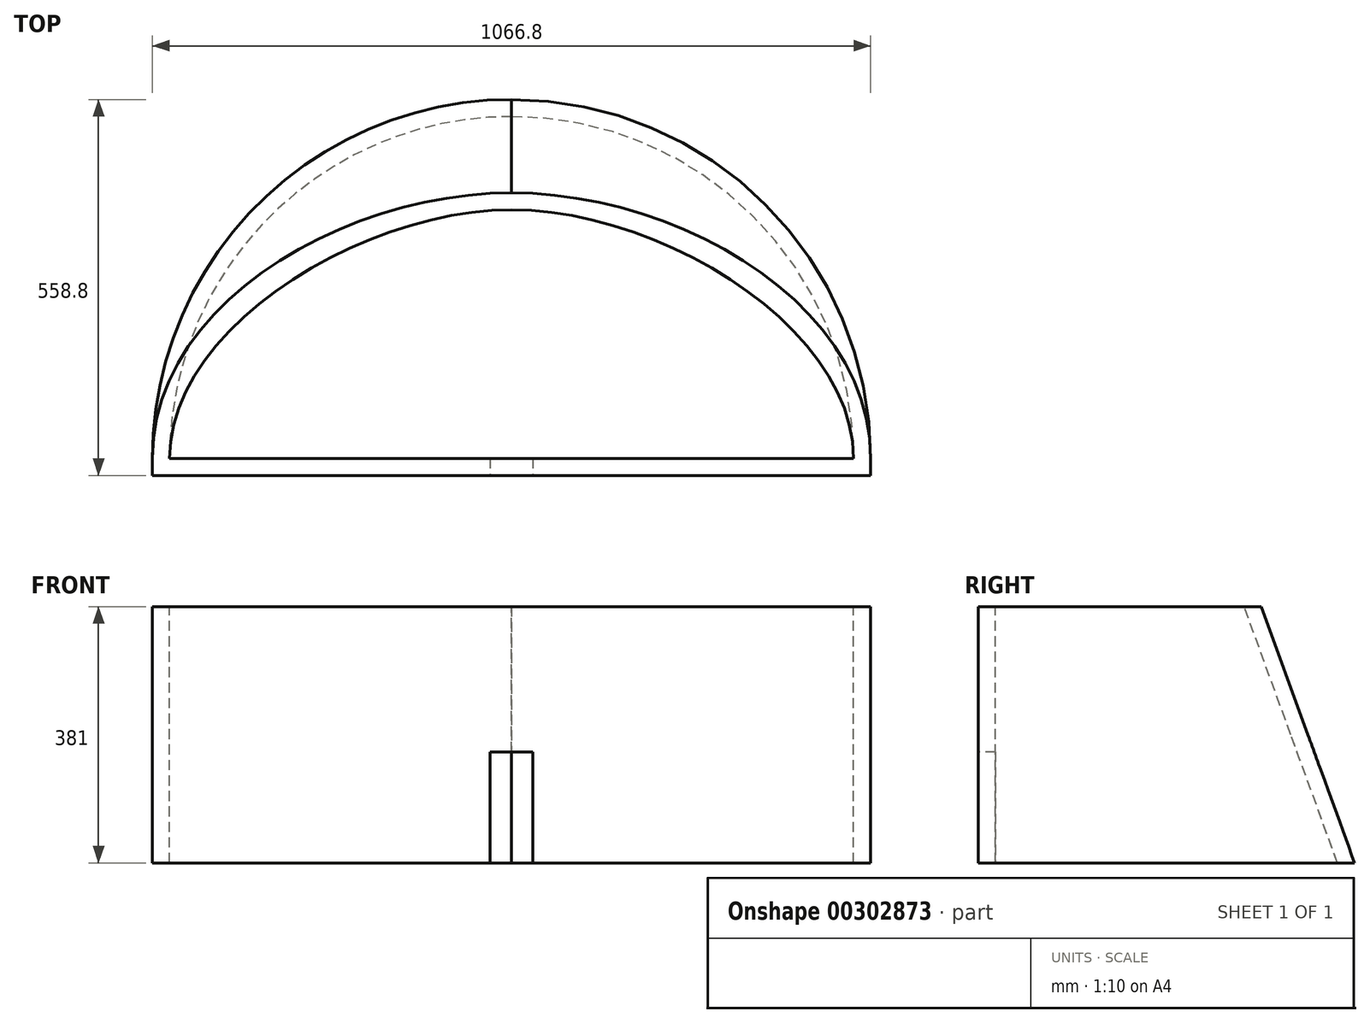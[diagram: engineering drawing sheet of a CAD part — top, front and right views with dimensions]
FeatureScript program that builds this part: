
annotation { "Feature Type Name" : "Feature", "Feature Type Description" : "" }
export const myFeature = defineFeature(function(context is Context, id is Id, definition is map)
    precondition{}
    {
        {
            var Q0;
            Q0=qCreatedBy(makeId("Right.planeOp"),FACE);
            var sketch = newSketch(context, id + "F0", { "sketchPlane" : qUnion([Q0])});
            skLineSegment(sketch, "E0", {"start": v(0, 0) * mm, "end": v(0, 323.57) * mm});
            skLineSegment(sketch, "E1", {"start": v(508, 0) * mm, "end": v(369.33, 381) * mm});
            skLineSegment(sketch, "E2", {"start": v(369.33, 381) * mm, "end": v(394.73, 381) * mm});
            skLineSegment(sketch, "E3", {"start": v(394.73, 381) * mm, "end": v(533.4, 0) * mm});
            skLineSegment(sketch, "E4", {"start": v(508, 0) * mm, "end": v(533.4, 0) * mm});
            skSolve(sketch);
        }
        {
            var Q0;
            Q0=qCreatedBy(makeId("Front.planeOp"),FACE);
            var sketch = newSketch(context, id + "F1", { "sketchPlane" : qUnion([Q0])});
            skLineSegment(sketch, "E5", {"start": v(508, 0) * mm, "end": v(508, 381) * mm});
            skLineSegment(sketch, "E6", {"start": v(508, 381) * mm, "end": v(533.4, 381) * mm});
            skLineSegment(sketch, "E7", {"start": v(533.4, 381) * mm, "end": v(533.4, 0) * mm});
            skLineSegment(sketch, "E8", {"start": v(533.4, 0) * mm, "end": v(508, 0) * mm});
            skSolve(sketch);
        }
        {
            var Q0;
            Q0=qCreatedBy(makeId("Top.planeOp"),FACE);
            var sketch = newSketch(context, id + "F2", { "sketchPlane" : qUnion([Q0])});
            skArc(sketch, "E9", {"start": v(533.4, 0) * mm, "mid": v(377.17, 377.17) * mm, "end": v(0, 533.4) * mm});
            skArc(sketch, "E10", {"start": v(508, 0) * mm, "mid": v(359.21, 359.21) * mm, "end": v(0, 508) * mm});
            skSolve(sketch);
        }
        {
            var Q0;
            Q0=qCreatedBy(makeId("Top.planeOp"),FACE);
            cPlane(context, id + "F3", {"entities" : qUnion([Q0]), "cplaneType" : CPlaneType.OFFSET, "offset" : 381 * mm, "width" : 152.4 * mm, "height" : 152.4 * mm});
        }
        {
            var Q0;
            Q0=qCreatedBy(id+"F3.planeOp",FACE);
            var sketch = newSketch(context, id + "F4", { "sketchPlane" : qUnion([Q0])});
            skFitSpline(sketch, "E11", {"points": [v(0, 369.33) * mm, v(508, 0) * mm], "startDerivative": vector(669.84, 0) * mm, "endDerivative": vector(0, -581.14) * mm});
            skFitSpline(sketch, "E12", {"points": [v(0, 394.73) * mm, v(533.4, 0) * mm], "startDerivative": vector(727.54, 0) * mm, "endDerivative": vector(0, -701.2) * mm});
            skSolve(sketch);
        }
        {
            var Q0;
            Q0=makeQuery(id+"F0.imprint","IMPRINT",FACE,{"disambiguationData":[TD([[makeQuery(id+"F0.imprint","IMPRINT",EDGE,{"derivedFrom":sQuery(id+"F0.wireOp",EDGE,"E1")}),-1.0]])]});
            var Q1;
            Q1=makeQuery(id+"F1.imprint","IMPRINT",FACE,{"disambiguationData":[TD([[makeQuery(id+"F1.imprint","IMPRINT",EDGE,{"derivedFrom":sQuery(id+"F1.wireOp",EDGE,"E5")}),-1.0]])]});
            var Q2;
            Q2=sQuery(id+"F4.wireOp",EDGE,"E11");
            var Q3;
            Q3=sQuery(id+"F4.wireOp",EDGE,"E12");
            var Q4;
            Q4=sQuery(id+"F2.wireOp",EDGE,"E10");
            var Q5;
            Q5=sQuery(id+"F2.wireOp",EDGE,"E9");
            loft(context, id + "F5", {"addGuides" : true, "sheetProfilesArray" : [{ "sheetProfileEntities" : qUnion([Q0]) }, { "sheetProfileEntities" : qUnion([Q1]) }], "guidesArray" : [{ "guideEntities" : qUnion([Q2]), "guideDerivativeType" : LoftGuideDerivativeType.DEFAULT, "guideDerivativeMagnitude" : 1 }, { "guideEntities" : qUnion([Q3]), "guideDerivativeType" : LoftGuideDerivativeType.DEFAULT, "guideDerivativeMagnitude" : 1 }, { "guideEntities" : qUnion([Q4]), "guideDerivativeType" : LoftGuideDerivativeType.DEFAULT, "guideDerivativeMagnitude" : 1 }, { "guideEntities" : qUnion([Q5]), "guideDerivativeType" : LoftGuideDerivativeType.DEFAULT, "guideDerivativeMagnitude" : 1 }]});
        }
        {
            var Q0;
            Q0=makeQuery(id+"F5.opLoft","SWEPT_BODY",BODY,{"disambiguationData":[OSD([makeQuery(id+"F0.imprint","IMPRINT",FACE,{"disambiguationData":[TD([[makeQuery(id+"F0.imprint","IMPRINT",EDGE,{"derivedFrom":sQuery(id+"F0.wireOp",EDGE,"E1")}),-1.0]])]}),makeQuery(id+"F1.imprint","IMPRINT",FACE,{"disambiguationData":[TD([[makeQuery(id+"F1.imprint","IMPRINT",EDGE,{"derivedFrom":sQuery(id+"F1.wireOp",EDGE,"E5")}),-1.0]])]}),sQuery(id+"F2.wireOp",EDGE,"E9"),sQuery(id+"F2.wireOp",EDGE,"E10"),sQuery(id+"F4.wireOp",EDGE,"E11"),sQuery(id+"F4.wireOp",EDGE,"E12")])]});
            var Q1;
            Q1=qCreatedBy(makeId("Right.planeOp"),FACE);
            mirror(context, id + "F6", {"operationType" : NewBodyOperationType.ADD, "entities" : qUnion([Q0]), "mirrorPlane" : qUnion([Q1])});
        }
        {
            var Q0;
            Q0=qCreatedBy(makeId("Top.planeOp"),FACE);
            var sketch = newSketch(context, id + "F7", { "sketchPlane" : qUnion([Q0])});
            skLineSegment(sketch, "E13.bottom", {"start": v(-533.4, 0) * mm, "end": v(533.4, 0) * mm});
            skLineSegment(sketch, "E13.top", {"start": v(-533.4, -25.4) * mm, "end": v(533.4, -25.4) * mm});
            skLineSegment(sketch, "E13.left", {"start": v(-533.4, 0) * mm, "end": v(-533.4, -25.4) * mm});
            skLineSegment(sketch, "E13.right", {"start": v(533.4, 0) * mm, "end": v(533.4, -25.4) * mm});
            skSolve(sketch);
        }
        {
            var Q0;
            Q0=makeQuery(id+"F7.imprint","IMPRINT",FACE,{"disambiguationData":[TD([[makeQuery(id+"F7.imprint","IMPRINT",EDGE,{"derivedFrom":sQuery(id+"F7.wireOp",EDGE,"E13.bottom")}),-1.0]])]});
            extrude(context, id + "F8", {"entities" : qUnion([Q0]), "operationType" : NewBodyOperationType.ADD, "depth" : 381 * mm});
        }
        {
            var Q0;
            Q0=makeQuery(id+"F8.opExtrude","SWEPT_FACE",FACE,{"disambiguationData":[OSD([sQuery(id+"F7.wireOp",EDGE,"E13.top")])]});
            var sketch = newSketch(context, id + "F9", { "sketchPlane" : qUnion([Q0])});
            skLineSegment(sketch, "E14.bottom", {"start": v(31.75, 165.1) * mm, "end": v(-31.75, 165.1) * mm});
            skLineSegment(sketch, "E14.top", {"start": v(31.75, 0) * mm, "end": v(-31.75, 0) * mm});
            skLineSegment(sketch, "E14.left", {"start": v(31.75, 165.1) * mm, "end": v(31.75, 0) * mm});
            skLineSegment(sketch, "E14.right", {"start": v(-31.75, 165.1) * mm, "end": v(-31.75, 0) * mm});
            skPoint(sketch, "E14.middle", {"position": v(0, 82.55) * mm});
            skSolve(sketch);
        }
        {
            var Q0;
            Q0 = qSketchRegion(id + "F9", true);
            extrude(context, id + "F10", {"entities" : qUnion([Q0]), "operationType" : NewBodyOperationType.REMOVE, "oppositeDirection" : true, "depth" : 25.4 * mm});
        }
    });
